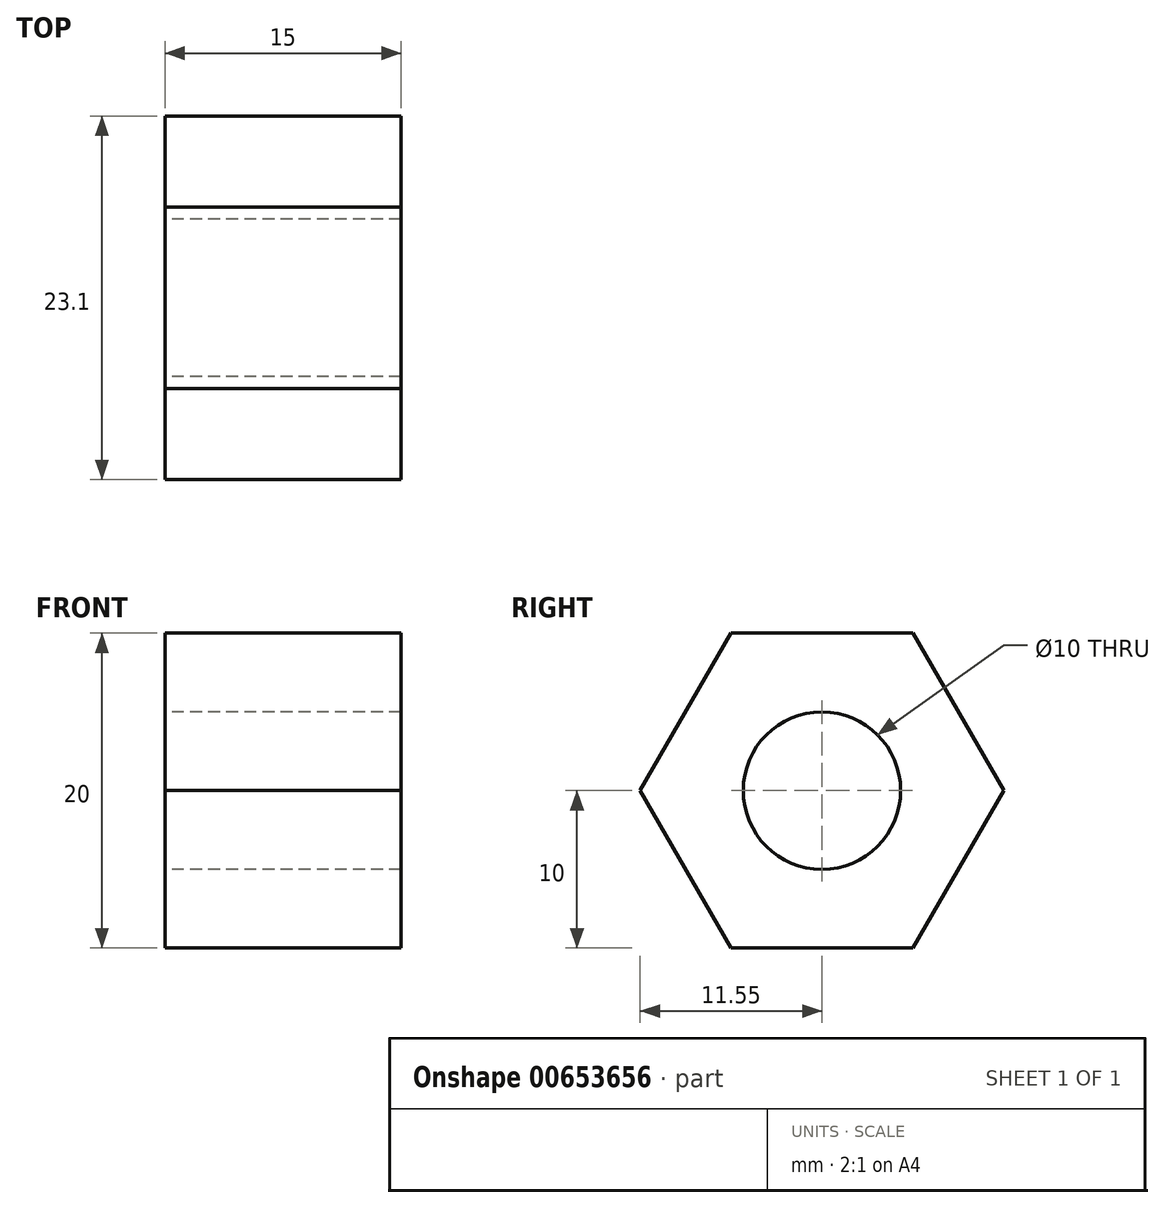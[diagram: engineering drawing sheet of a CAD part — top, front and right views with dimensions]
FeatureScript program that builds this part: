
annotation { "Feature Type Name" : "Feature", "Feature Type Description" : "" }
export const myFeature = defineFeature(function(context is Context, id is Id, definition is map)
    precondition{}
    {
        {
            var Q0;
            Q0=qCreatedBy(makeId("Right.planeOp"),FACE);
            var sketch = newSketch(context, id + "F0", { "sketchPlane" : qUnion([Q0])});
            skCircle(sketch, "E0.cCircle", {"center": v(0, 0) * mm, "radius": 10 * mm, "construction": true});
            skLineSegment(sketch, "E0.0", {"start": v(-5.77, 10) * mm, "end": v(5.77, 10) * mm});
            skLineSegment(sketch, "E0.1", {"start": v(5.77, 10) * mm, "end": v(11.55, 0) * mm});
            skLineSegment(sketch, "E0.2", {"start": v(11.55, 0) * mm, "end": v(5.77, -10) * mm});
            skLineSegment(sketch, "E0.3", {"start": v(5.77, -10) * mm, "end": v(-5.77, -10) * mm});
            skLineSegment(sketch, "E0.4", {"start": v(-5.77, -10) * mm, "end": v(-11.55, 0) * mm});
            skLineSegment(sketch, "E0.5", {"start": v(-11.55, 0) * mm, "end": v(-5.77, 10) * mm});
            skPoint(sketch, "E0.0.midPoint", {"position": v(0, 10) * mm});
            skCircle(sketch, "E1", {"center": v(0, 0) * mm, "radius": 5 * mm});
            skSolve(sketch);
        }
        {
            var Q0;
            Q0 = qSketchRegion(id + "F0", true);
            extrude(context, id + "F1", {"entities" : qUnion([Q0]), "depth" : 15 * mm, "offsetDistance" : 25 * mm});
        }
    });
